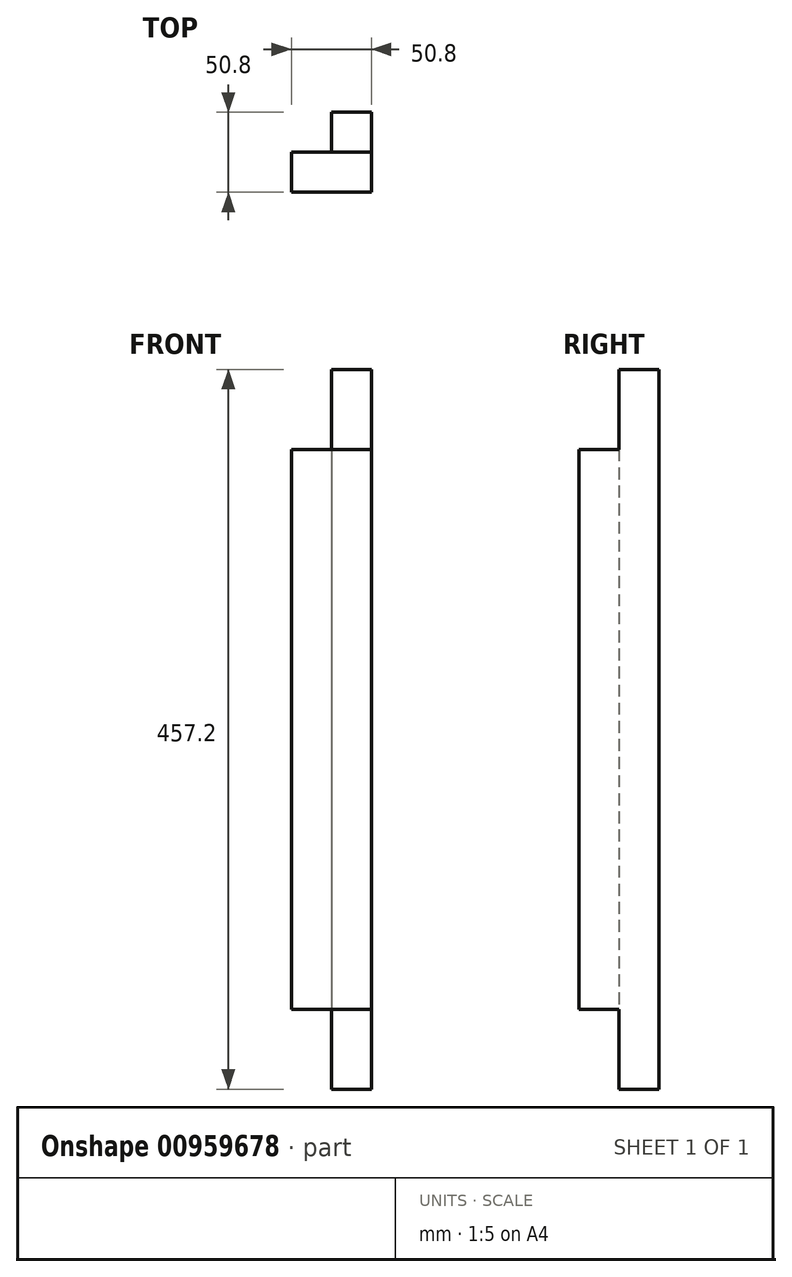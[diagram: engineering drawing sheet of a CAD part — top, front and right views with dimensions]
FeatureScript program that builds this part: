
annotation { "Feature Type Name" : "Feature", "Feature Type Description" : "" }
export const myFeature = defineFeature(function(context is Context, id is Id, definition is map)
    precondition{}
    {
        {
            var Q0;
            Q0=qCreatedBy(makeId("Top.planeOp"),FACE);
            var sketch = newSketch(context, id + "F0", { "sketchPlane" : qUnion([Q0])});
            skLineSegment(sketch, "E0.top", {"start": v(-83, -49.63) * mm, "end": v(-32.2, -49.63) * mm});
            skLineSegment(sketch, "E0.right", {"start": v(-32.2, 1.17) * mm, "end": v(-32.2, -49.63) * mm});
            skLineSegment(sketch, "E1", {"start": v(-57.6, 1.17) * mm, "end": v(-57.6, -24.23) * mm});
            skLineSegment(sketch, "E2", {"start": v(-57.6, -24.23) * mm, "end": v(-83, -24.23) * mm});
            skLineSegment(sketch, "E3", {"start": v(-83, -49.63) * mm, "end": v(-83, -24.23) * mm});
            skLineSegment(sketch, "E4", {"start": v(-57.6, 1.17) * mm, "end": v(-32.2, 1.17) * mm});
            skSolve(sketch);
        }
        {
            var Q0;
            Q0=makeQuery(id+"F0.imprint","IMPRINT",FACE,{"disambiguationData":[TD([[makeQuery(id+"F0.imprint","IMPRINT",EDGE,{"derivedFrom":sQuery(id+"F0.wireOp",EDGE,"E0.top")}),1.0]])]});
            extrude(context, id + "F1", {"entities" : qUnion([Q0]), "depth" : 457.2 * mm, "offsetDistance" : 25.4 * mm});
        }
        {
            var Q0;
            Q0=makeQuery(id+"F1.opExtrude","SWEPT_FACE",FACE,{"disambiguationData":[OSD([sQuery(id+"F0.wireOp",EDGE,"E0.top")])]});
            var sketch = newSketch(context, id + "F2", { "sketchPlane" : qUnion([Q0])});
            skLineSegment(sketch, "E5.bottom", {"start": v(-83, 0) * mm, "end": v(-32.2, 0) * mm});
            skLineSegment(sketch, "E5.top", {"start": v(-83, 50.8) * mm, "end": v(-32.2, 50.8) * mm});
            skLineSegment(sketch, "E5.left", {"start": v(-83, 0) * mm, "end": v(-83, 50.8) * mm});
            skLineSegment(sketch, "E5.right", {"start": v(-32.2, 0) * mm, "end": v(-32.2, 50.8) * mm});
            skLineSegment(sketch, "E6.bottom", {"start": v(-83, 457.2) * mm, "end": v(-32.2, 457.2) * mm});
            skLineSegment(sketch, "E6.top", {"start": v(-83, 406.4) * mm, "end": v(-32.2, 406.4) * mm});
            skLineSegment(sketch, "E6.left", {"start": v(-83, 457.2) * mm, "end": v(-83, 406.4) * mm});
            skLineSegment(sketch, "E6.right", {"start": v(-32.2, 457.2) * mm, "end": v(-32.2, 406.4) * mm});
            skSolve(sketch);
        }
        {
            var Q0;
            Q0=makeQuery(id+"F2.imprint","IMPRINT",FACE,{"disambiguationData":[TD([[makeQuery(id+"F2.imprint","IMPRINT",EDGE,{"derivedFrom":sQuery(id+"F2.wireOp",EDGE,"E6.bottom")}),-1.0]])]});
            var Q1;
            Q1=makeQuery(id+"F2.imprint","IMPRINT",FACE,{"disambiguationData":[TD([[makeQuery(id+"F2.imprint","IMPRINT",EDGE,{"derivedFrom":sQuery(id+"F2.wireOp",EDGE,"E5.bottom")}),1.0]])]});
            extrude(context, id + "F3", {"entities" : qUnion([Q0, Q1]), "operationType" : NewBodyOperationType.REMOVE, "oppositeDirection" : true, "depth" : 25.4 * mm, "offsetDistance" : 25.4 * mm});
        }
    });
